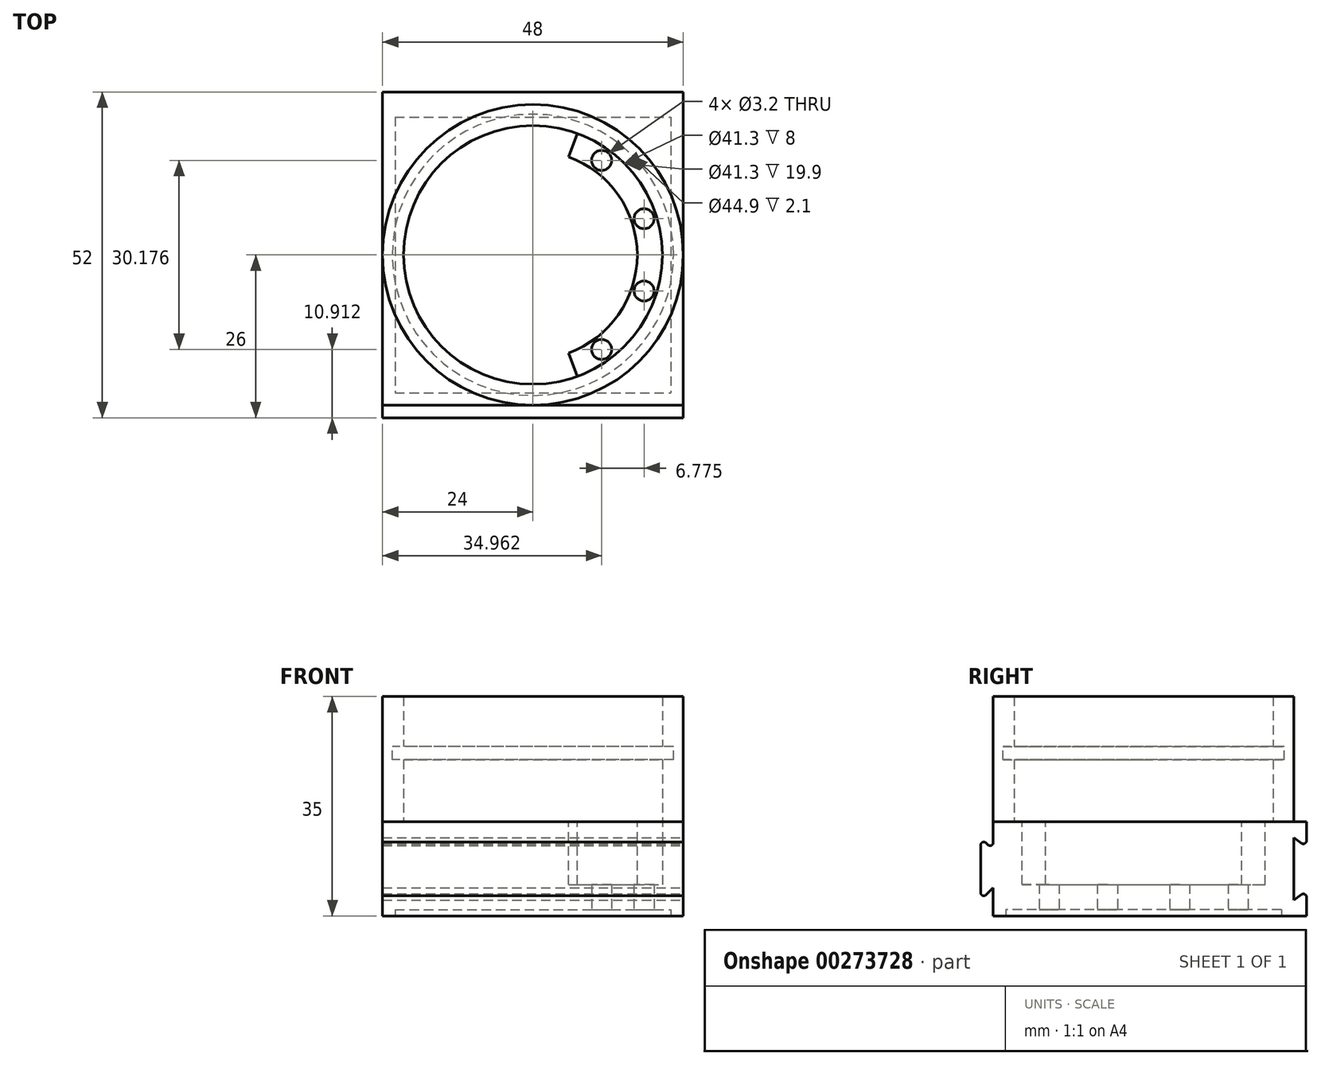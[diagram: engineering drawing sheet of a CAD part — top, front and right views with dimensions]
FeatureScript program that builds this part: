
annotation { "Feature Type Name" : "Feature", "Feature Type Description" : "" }
export const myFeature = defineFeature(function(context is Context, id is Id, definition is map)
    precondition{}
    {
        {
            var Q0;
            Q0=qCreatedBy(makeId("Top.planeOp"),FACE);
            var sketch = newSketch(context, id + "F0", { "sketchPlane" : qUnion([Q0])});
            skCircle(sketch, "E0", {"center": v(0, 0) * mm, "radius": 20.65 * mm});
            skCircle(sketch, "E1", {"center": v(0, 0) * mm, "radius": 24 * mm});
            skLineSegment(sketch, "E2.bottom", {"start": v(-24, 24) * mm, "end": v(24, 24) * mm});
            skLineSegment(sketch, "E2.top", {"start": v(-24, -24) * mm, "end": v(24, -24) * mm});
            skLineSegment(sketch, "E2.left", {"start": v(-24, 24) * mm, "end": v(-24, -24) * mm});
            skLineSegment(sketch, "E2.right", {"start": v(24, 24) * mm, "end": v(24, -24) * mm});
            skPoint(sketch, "E3", {"position": v(0, 24) * mm});
            skPoint(sketch, "E4", {"position": v(-24, 0) * mm});
            skSolve(sketch);
        }
        {
            var Q0;
            Q0=makeQuery(id+"F0.imprint","IMPRINT",FACE,{"disambiguationData":[TD([[makeQuery(id+"F0.imprint","IMPRINT",EDGE,{"derivedFrom":sQuery(id+"F0.wireOp",EDGE,"E1")}),-1.0]])]});
            var Q1;
            Q1=makeQuery(id+"F0.imprint","IMPRINT",FACE,{"disambiguationData":[TD([[makeQuery(id+"F0.imprint","IMPRINT",EDGE,{"derivedFrom":sQuery(id+"F0.wireOp",EDGE,"E0")}),-1.0]])]});
            var Q2;
            Q2=makeQuery(id+"F0.imprint","IMPRINT",FACE,{"disambiguationData":[TD([[makeQuery(id+"F0.imprint","IMPRINT",EDGE,{"derivedFrom":sQuery(id+"F0.wireOp",EDGE,"E0")}),1.0]])]});
            extrude(context, id + "F1", {"entities" : qUnion([Q0, Q1, Q2]), "oppositeDirection" : true, "depth" : 15 * mm});
        }
        {
            var Q0;
            Q0=makeQuery(id+"F0.imprint","IMPRINT",FACE,{"disambiguationData":[TD([[makeQuery(id+"F0.imprint","IMPRINT",EDGE,{"derivedFrom":sQuery(id+"F0.wireOp",EDGE,"E0")}),-1.0]])]});
            extrude(context, id + "F2", {"entities" : qUnion([Q0]), "operationType" : NewBodyOperationType.ADD, "depth" : 20 * mm});
        }
        {
            var Q0;
            Q0=makeQuery(id+"F1.opExtrude","CAP_FACE",FACE,{"disambiguationData":[OSD([sQuery(id+"F0.wireOp",EDGE,"E2.bottom"),sQuery(id+"F0.wireOp",EDGE,"E2.top"),sQuery(id+"F0.wireOp",EDGE,"E2.left"),sQuery(id+"F0.wireOp",EDGE,"E2.right")])],"isStart":false});
            var sketch = newSketch(context, id + "F3", { "sketchPlane" : qUnion([Q0])});
            skLineSegment(sketch, "E5.0", {"start": v(-22, 22) * mm, "end": v(22, 22) * mm});
            skLineSegment(sketch, "E5.1", {"start": v(-22, -22) * mm, "end": v(-22, 22) * mm});
            skLineSegment(sketch, "E5.2", {"start": v(-22, -22) * mm, "end": v(22, -22) * mm});
            skLineSegment(sketch, "E5.3", {"start": v(22, -22) * mm, "end": v(22, 22) * mm});
            skSolve(sketch);
        }
        {
            var Q0;
            Q0=makeQuery(id+"F3.imprint","IMPRINT",FACE,{"disambiguationData":[TD([[makeQuery(id+"F3.imprint","IMPRINT",EDGE,{"derivedFrom":sQuery(id+"F3.wireOp",EDGE,"E5.0")}),-1.0]])]});
            var Q1;
            {var subQ0=sQuery(id+"F0.wireOp",EDGE,"E2.right");var subQ1=sQuery(id+"F0.wireOp",EDGE,"E2.left");var subQ2=sQuery(id+"F0.wireOp",EDGE,"E2.top");var subQ3=sQuery(id+"F0.wireOp",EDGE,"E2.bottom");Q1=makeQuery(id+"F2.boolean.opBoolean","SPLIT",FACE,{"disambiguationData":[TD([makeQuery(id+"F1.opExtrude","SWEPT_FACE",FACE,{"disambiguationData":[OSD([subQ3])]})])],"derivedFrom":makeQuery(id+"F1.opExtrude","CAP_FACE",FACE,{"disambiguationData":[OSD([subQ3,subQ2,subQ1,subQ0])],"isStart":true})});}
            extrude(context, id + "F4", {"entities" : qUnion([Q0]), "operationType" : NewBodyOperationType.REMOVE, "oppositeDirection" : true, "endBoundEntityFace" : qUnion([Q1]), "depth" : 1 * mm});
        }
        {
            var Q0;
            Q0=makeQuery(id+"F4.boolean.opBoolean","COPY",FACE,{"derivedFrom":makeQuery(id+"F4.opExtrude","CAP_FACE",FACE,{"disambiguationData":[OSD([sQuery(id+"F3.wireOp",EDGE,"E5.0"),sQuery(id+"F3.wireOp",EDGE,"E5.1"),sQuery(id+"F3.wireOp",EDGE,"E5.2"),sQuery(id+"F3.wireOp",EDGE,"E5.3")])],"isStart":false})});
            var sketch = newSketch(context, id + "F5", { "sketchPlane" : qUnion([Q0])});
            skCircle(sketch, "E6.0", {"center": v(0, 0) * mm, "radius": 20.65 * mm});
            skCircle(sketch, "E7", {"center": v(0, 18.65) * mm, "radius": 1.6 * mm});
            skCircle(sketch, "E8.1.0", {"center": v(10.96, 15.09) * mm, "radius": 1.6 * mm});
            skCircle(sketch, "E8.2.0", {"center": v(17.74, 5.76) * mm, "radius": 1.6 * mm});
            skCircle(sketch, "E8.3.0", {"center": v(17.74, -5.76) * mm, "radius": 1.6 * mm});
            skCircle(sketch, "E8.4.0", {"center": v(10.96, -15.09) * mm, "radius": 1.6 * mm});
            skCircle(sketch, "E8.5.0", {"center": v(0, -18.65) * mm, "radius": 1.6 * mm});
            skLineSegment(sketch, "E8.anchor1", {"start": v(0, 0) * mm, "end": v(0, 18.65) * mm, "construction": true});
            skLineSegment(sketch, "E8.anchor2", {"start": v(0, 0) * mm, "end": v(0, -18.65) * mm, "construction": true});
            skSolve(sketch);
        }
        {
            var Q0;
            Q0=makeQuery(id+"F5.imprint","IMPRINT",FACE,{"disambiguationData":[TD([[makeQuery(id+"F5.imprint","IMPRINT",EDGE,{"derivedFrom":sQuery(id+"F5.wireOp",EDGE,"E8.1.0")}),1.0]])]});
            var Q1;
            Q1=makeQuery(id+"F5.imprint","IMPRINT",FACE,{"disambiguationData":[TD([[makeQuery(id+"F5.imprint","IMPRINT",EDGE,{"derivedFrom":sQuery(id+"F5.wireOp",EDGE,"E8.2.0")}),1.0]])]});
            var Q2;
            Q2=makeQuery(id+"F5.imprint","IMPRINT",FACE,{"disambiguationData":[TD([[makeQuery(id+"F5.imprint","IMPRINT",EDGE,{"derivedFrom":sQuery(id+"F5.wireOp",EDGE,"E8.3.0")}),1.0]])]});
            var Q3;
            Q3=makeQuery(id+"F5.imprint","IMPRINT",FACE,{"disambiguationData":[TD([[makeQuery(id+"F5.imprint","IMPRINT",EDGE,{"derivedFrom":sQuery(id+"F5.wireOp",EDGE,"E8.4.0")}),1.0]])]});
            extrude(context, id + "F6", {"entities" : qUnion([Q0, Q1, Q2, Q3]), "operationType" : NewBodyOperationType.REMOVE, "oppositeDirection" : true, "depth" : 25 * mm});
        }
        {
            var Q0;
            Q0=makeQuery(id+"F1.opExtrude","SWEPT_FACE",FACE,{"disambiguationData":[OSD([sQuery(id+"F0.wireOp",EDGE,"E2.right")])]});
            var sketch = newSketch(context, id + "F7", { "sketchPlane" : qUnion([Q0])});
            skLineSegment(sketch, "E9", {"start": v(-24, -10.5) * mm, "end": v(-26, -12.5) * mm});
            skLineSegment(sketch, "E10", {"start": v(-26, -12.5) * mm, "end": v(-26, -2.5) * mm});
            skLineSegment(sketch, "E11", {"start": v(-26, -2.5) * mm, "end": v(-24, -4.5) * mm});
            skLineSegment(sketch, "E12", {"start": v(24, -15) * mm, "end": v(26, -15) * mm});
            skLineSegment(sketch, "E13", {"start": v(26, -15) * mm, "end": v(26, 0) * mm});
            skLineSegment(sketch, "E14", {"start": v(26, 0) * mm, "end": v(24, 0) * mm});
            skLineSegment(sketch, "E15", {"start": v(26, -11) * mm, "end": v(24, -12.5) * mm});
            skLineSegment(sketch, "E16", {"start": v(24, -12.5) * mm, "end": v(24, -2.5) * mm});
            skLineSegment(sketch, "E17", {"start": v(24, -2.5) * mm, "end": v(26, -4) * mm});
            skPoint(sketch, "E18", {"position": v(24, -7.5) * mm});
            skPoint(sketch, "E19", {"position": v(-24, -7.5) * mm});
            skSolve(sketch);
        }
        {
            var Q0;
            {var subQ0=sQuery(id+"F7.wireOp",EDGE,"E9");Q0=makeQuery(id+"F7.imprint","IMPRINT",FACE,{"disambiguationData":[TD([[makeQuery(id+"F7.imprint","IMPRINT",EDGE,{"derivedFrom":subQ0}),-1.0]])]});}
            var Q1;
            {var subQ0=sQuery(id+"F7.wireOp",EDGE,"E12");Q1=makeQuery(id+"F7.imprint","IMPRINT",FACE,{"disambiguationData":[TD([[makeQuery(id+"F7.imprint","IMPRINT",EDGE,{"derivedFrom":subQ0}),1.0]])]});}
            var Q2;
            {var subQ0=sQuery(id+"F7.wireOp",EDGE,"E14");Q2=makeQuery(id+"F7.imprint","IMPRINT",FACE,{"disambiguationData":[TD([[makeQuery(id+"F7.imprint","IMPRINT",EDGE,{"derivedFrom":subQ0}),1.0]])]});}
            var Q3;
            Q3=makeQuery(id+"F1.opExtrude","SWEPT_FACE",FACE,{"disambiguationData":[OSD([sQuery(id+"F0.wireOp",EDGE,"E2.left")])]});
            extrude(context, id + "F8", {"entities" : qUnion([Q0, Q1, Q2]), "operationType" : NewBodyOperationType.ADD, "endBound" : BoundingType.UP_TO_SURFACE, "oppositeDirection" : true, "endBoundEntityFace" : qUnion([Q3]), "depth" : 25 * mm});
        }
        {
            var Q0;
            Q0=makeQuery(id+"F8.opExtrude","SWEPT_EDGE",EDGE,{"disambiguationData":[OSD([sQuery(id+"F0.wireOp",EDGE,"E2.top"),sQuery(id+"F0.wireOp",EDGE,"E2.right"),sQuery(id+"F7.wireOp",EDGE,"E9")])]});
            var Q1;
            Q1=makeQuery(id+"F8.opExtrude","SWEPT_EDGE",EDGE,{"disambiguationData":[OSD([sQuery(id+"F7.wireOp",EDGE,"E9"),sQuery(id+"F7.wireOp",EDGE,"E10")])]});
            var Q2;
            Q2=makeQuery(id+"F8.opExtrude","SWEPT_EDGE",EDGE,{"disambiguationData":[OSD([sQuery(id+"F7.wireOp",EDGE,"E10"),sQuery(id+"F7.wireOp",EDGE,"E11")])]});
            var Q3;
            Q3=makeQuery(id+"F8.opExtrude","SWEPT_EDGE",EDGE,{"disambiguationData":[OSD([sQuery(id+"F0.wireOp",EDGE,"E2.top"),sQuery(id+"F0.wireOp",EDGE,"E2.right"),sQuery(id+"F7.wireOp",EDGE,"E11")])]});
            var Q4;
            Q4=makeQuery(id+"F8.opExtrude","SWEPT_EDGE",EDGE,{"disambiguationData":[OSD([sQuery(id+"F0.wireOp",EDGE,"E2.bottom"),sQuery(id+"F0.wireOp",EDGE,"E2.right"),sQuery(id+"F7.wireOp",EDGE,"E16"),sQuery(id+"F7.wireOp",EDGE,"E17")])]});
            var Q5;
            Q5=makeQuery(id+"F8.opExtrude","SWEPT_EDGE",EDGE,{"disambiguationData":[OSD([sQuery(id+"F7.wireOp",EDGE,"E13"),sQuery(id+"F7.wireOp",EDGE,"E17")])]});
            var Q6;
            Q6=makeQuery(id+"F8.opExtrude","SWEPT_EDGE",EDGE,{"disambiguationData":[OSD([sQuery(id+"F0.wireOp",EDGE,"E2.bottom"),sQuery(id+"F0.wireOp",EDGE,"E2.right"),sQuery(id+"F7.wireOp",EDGE,"E15"),sQuery(id+"F7.wireOp",EDGE,"E16")])]});
            var Q7;
            Q7=makeQuery(id+"F8.opExtrude","SWEPT_EDGE",EDGE,{"disambiguationData":[OSD([sQuery(id+"F7.wireOp",EDGE,"E13"),sQuery(id+"F7.wireOp",EDGE,"E15")])]});
            fillet(context, id + "F9", {"entities" : qUnion([Q0, Q1, Q2, Q3, Q4, Q5, Q6, Q7]), "radius" : 0.5 * mm, "tangentPropagation" : true, "allowEdgeOverflow" : false});
        }
        {
            var Q0;
            Q0=qCreatedBy(makeId("Front.planeOp"),FACE);
            var sketch = newSketch(context, id + "F10", { "sketchPlane" : qUnion([Q0])});
            skLineSegment(sketch, "E20.0", {"start": v(-20.65, 20) * mm, "end": v(20.65, 20) * mm});
            skLineSegment(sketch, "E21", {"start": v(-20.65, 20) * mm, "end": v(-20.65, 12) * mm, "construction": true});
            skLineSegment(sketch, "E22", {"start": v(-20.65, 12) * mm, "end": v(-22.45, 12) * mm});
            skLineSegment(sketch, "E23", {"start": v(-22.45, 12) * mm, "end": v(-22.45, 9.9) * mm});
            skLineSegment(sketch, "E24", {"start": v(-22.45, 9.9) * mm, "end": v(-20.65, 9.9) * mm});
            skLineSegment(sketch, "E25", {"start": v(-20.65, 9.9) * mm, "end": v(-20.65, 12) * mm});
            skSolve(sketch);
        }
        {
            var Q0;
            Q0=makeQuery(id+"F10.imprint","IMPRINT",FACE,{"disambiguationData":[TD([[makeQuery(id+"F10.imprint","IMPRINT",EDGE,{"derivedFrom":sQuery(id+"F10.wireOp",EDGE,"E22")}),1.0]])]});
            var Q1;
            Q1=makeQuery(id+"F2.opExtrude","CAP_EDGE",EDGE,{"disambiguationData":[OSD([sQuery(id+"F0.wireOp",EDGE,"E0")])],"isStart":false});
            revolve(context, id + "F11", {"operationType" : NewBodyOperationType.REMOVE, "entities" : qUnion([Q0]), "axis" : qUnion([Q1]), "revolveType" : RevolveType.FULL, "oppositeDirection" : true});
        }
        {
            var Q0;
            Q0=makeQuery(id+"F0.imprint","IMPRINT",FACE,{"disambiguationData":[TD([[makeQuery(id+"F0.imprint","IMPRINT",EDGE,{"derivedFrom":sQuery(id+"F0.wireOp",EDGE,"E0")}),1.0]])]});
            var sketch = newSketch(context, id + "F12", { "sketchPlane" : qUnion([Q0])});
            skCircle(sketch, "E26.0", {"center": v(0, 0) * mm, "radius": 20.65 * mm});
            skCircle(sketch, "E27.0", {"center": v(0, 0) * mm, "radius": 16.65 * mm});
            skLineSegment(sketch, "E28", {"start": v(0, 0) * mm, "end": v(7.06, -19.4) * mm});
            skLineSegment(sketch, "E29", {"start": v(0, 0) * mm, "end": v(7.06, 19.4) * mm});
            skSolve(sketch);
        }
        {
            var Q0;
            {var subQ0=sQuery(id+"F12.wireOp",EDGE,"E28");var subQ1=sQuery(id+"F12.wireOp",EDGE,"E26.0");var subQ2=makeQuery(id+"F12.imprint","INTERSECT",VERTEX,{"derivedFrom":[subQ1,subQ0]});Q0=makeQuery(id+"F12.imprint","IMPRINT",FACE,{"disambiguationData":[TD([[makeQuery(id+"F12.imprint","IMPRINT",EDGE,{"disambiguationData":[TD([[subQ2,-1.0]])],"derivedFrom":subQ1}),1.0]])]});}
            extrude(context, id + "F13", {"entities" : qUnion([Q0]), "operationType" : NewBodyOperationType.REMOVE, "oppositeDirection" : true, "depth" : 10 * mm});
        }
    });
